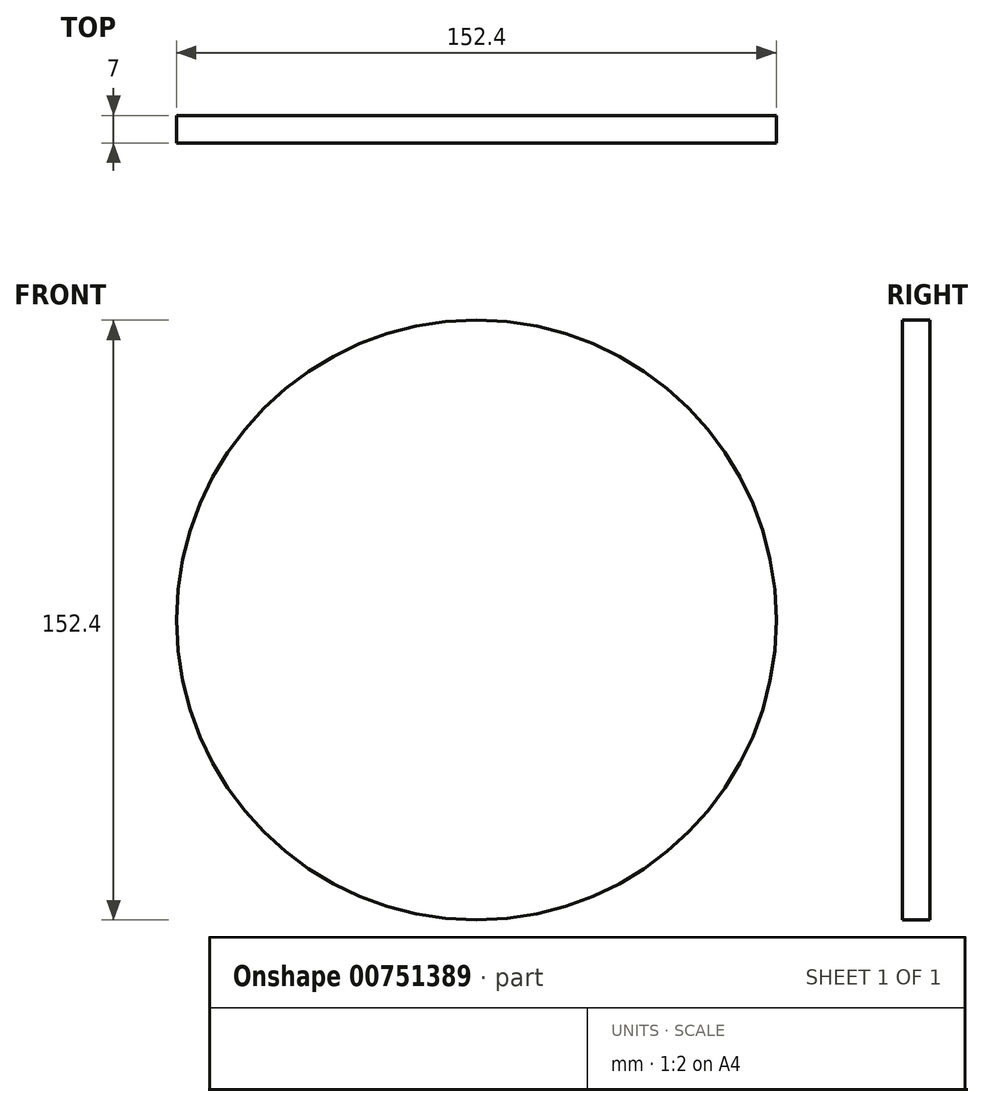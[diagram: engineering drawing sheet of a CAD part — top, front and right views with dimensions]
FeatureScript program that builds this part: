
annotation { "Feature Type Name" : "Feature", "Feature Type Description" : "" }
export const myFeature = defineFeature(function(context is Context, id is Id, definition is map)
    precondition{}
    {
        {
            assignVariable(context, id + "F0", {"name" : "thickness", "anyValue" : 7});
        }
        {
            var Q0;
            Q0=qCreatedBy(makeId("Front.planeOp"),FACE);
            var sketch = newSketch(context, id + "F1", { "sketchPlane" : qUnion([Q0])});
            skCircle(sketch, "E0", {"center": v(0, 0) * mm, "radius": 76.2 * mm});
            skSolve(sketch);
        }
        {
            var Q0;
            Q0=makeQuery(id+"F1.imprint","IMPRINT",FACE,{"disambiguationData":[TD([[makeQuery(id+"F1.imprint","IMPRINT",EDGE,{"derivedFrom":sQuery(id+"F1.wireOp",EDGE,"E0")}),1.0]])]});
            extrude(context, id + "F2", {"entities" : qUnion([Q0]), "depth" : (getVariable(context, 'thickness')) * mm, "offsetDistance" : 25.4 * mm});
        }
    });
